# Revit family: Фитинг_Weser_Муфта прямая переходная
name_source: partatom
category: Соединительные детали трубопроводов
units: mm (PartAtom-declared; Revit-internal decimal feet)

## family parameters
Всегда вертикально = Да
Заголовок OmniClass = Pipework Fittings
На основе рабочей плоскости = Нет
Номер OmniClass = 23.60.30.11.14
Общий = Нет
При загрузке вырезать с полостями = Нет
Размер круглого соединителя = Использовать диаметр
Тип детали = Переход

## types (1)
- Латунь
    ADSK_Единица измерения = шт.
    ADSK_Завод-изготовитель = Weser
    ADSK_Марка = WESERpex
    URL = https://www.weser.ru
    Материал = Латунь
    Метод определения потерь = Табличный коэффициент K
    Отметка по умолчанию = 0 мм
    Поиск в таблице имен = Фитинг_Weser_Муфта прямая переходная(Наименование)
    Поиск в таблице имен 2 = Фитинг_Weser_Муфта прямая переходная(Код)
    Таблица коэффициентов K = Сужающийся переходник/Сочленение/Соединение/Расширяющийся переходник

## geometry (parser evidence)
native form markers: Sweep x3
no freeform markers — native parametric forms only
